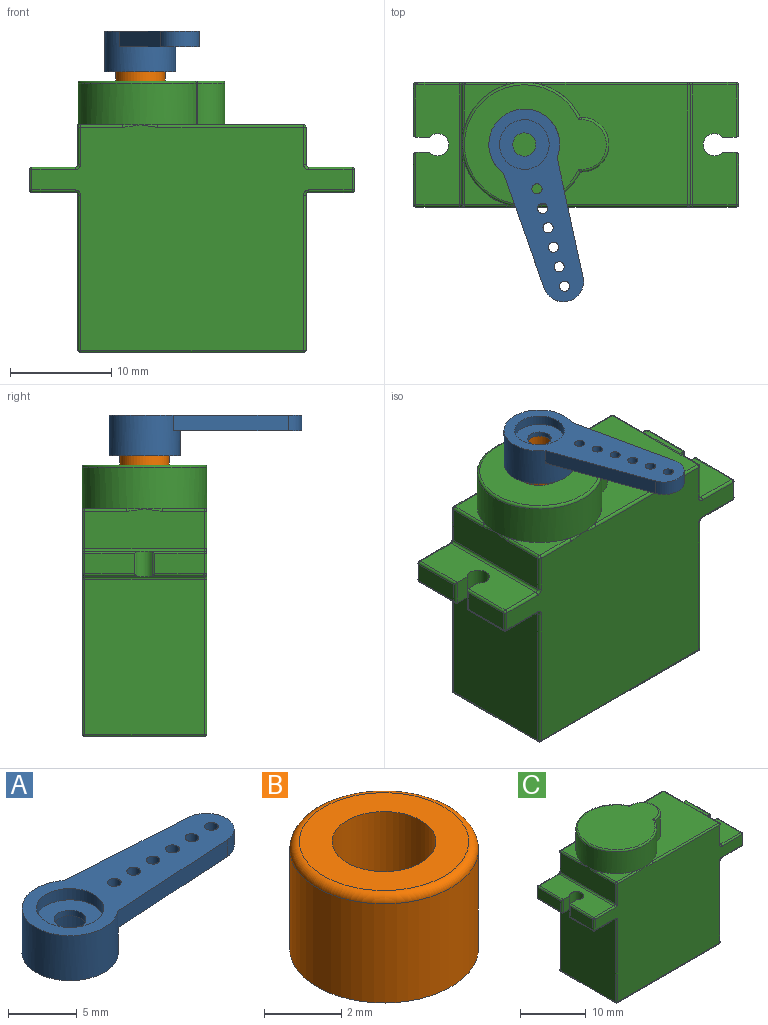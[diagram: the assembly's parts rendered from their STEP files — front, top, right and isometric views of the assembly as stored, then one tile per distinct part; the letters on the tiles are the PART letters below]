
ASSEMBLY  parts=3 mates=2
PART A: 18 faces, bbox 19.6x7x4 mm
  f0: plane 4.9x4.9mm, normal (0,0,-1), area 14.7mm2, adj f14,f16
  f1: plane 12.01x1.5mm, normal (0.06,1,0), area 18.1mm2, adj f2,f10,f12,f13
  f2: cylinder r=3.5mm len=7mm, axis (0,0,-1), area 78.5mm2, adj f1,f3,f12,f13,f17
  f3: plane 12.01x1.5mm, normal (0.06,-1,0), area 18.1mm2, adj f2,f10,f12,f13
  f4: cylinder r=0.5mm len=1.5mm, axis (0,0,-1), area 4.7mm2, adj f12,f13
  f5: cylinder r=0.5mm len=1.5mm, axis (0,0,-1), area 4.7mm2, adj f12,f13
  f6: cylinder r=0.5mm len=1.5mm, axis (0,0,-1), area 4.7mm2, adj f12,f13
  f7: cylinder r=0.5mm len=1.5mm, axis (0,0,-1), area 4.7mm2, adj f12,f13
  f8: cylinder r=0.5mm len=1.5mm, axis (0,0,-1), area 4.7mm2, adj f12,f13
  f9: cylinder r=0.5mm len=1.5mm, axis (0,0,-1), area 4.7mm2, adj f12,f13
  f10: cylinder r=2mm len=3.99mm, axis (0,0,-1), area 9mm2, adj f1,f3,f12,f13
  f11: cylinder r=2.45mm len=4.9mm, axis (0,0,-1), area 15.4mm2, adj f12,f15
  f12: plane 19.55x7mm, normal (0,0,1), area 72.6mm2, adj f1,f2,f3,f4,f5,f6,f7,f8
  f13: plane 13.89x5.5mm, normal (0,0,-1), area 53mm2, adj f1,f2,f3,f4,f5,f6,f7,f8
  f14: cylinder r=1.15mm len=2.3mm, axis (0,0,-1), area 3.6mm2, adj f0,f15
  f15: plane 4.9x4.9mm, normal (0,0,1), area 14.7mm2, adj f11,f14
  f16: cylinder r=2.45mm len=4.9mm, axis (0,0,1), area 38.5mm2, adj f0,f17
  f17: plane 7x7mm, normal (0,0,-1), area 19.6mm2, adj f2,f16
PART B: 5 faces, bbox 5.3x5.3x3.4 mm
  f0: cylinder r=1.35mm len=3.4mm, axis (0,0,-1), area 28.8mm2, adj f2,f3
  f1: cylinder r=2.45mm len=4.9mm, axis (0,0,-1), area 48.5mm2, adj f3,f4
  f2: plane 4.4x4.4mm, normal (0,0,1), area 9.5mm2, adj f0,f4
  f3: plane 4.9x4.9mm, normal (0,0,-1), area 13.1mm2, adj f0,f1
  f4: torus R=2.2mm, axis (0,0,1), area 5.8mm2, adj f1,f2
PART C: 110 faces, bbox 32.2x13.4x26.9 mm
  f0: plane 14.36x11.8mm, normal (0,0,1), area 121.3mm2, adj f24,f25,f26,f27,f34,f38,f39
  f1: plane 4.16x4.16mm, normal (0,0,1), area 5.7mm2, adj f25,f71,f72
  f2: plane 15.3x11.8mm, normal (-1,0,0), area 180.5mm2, adj f94,f95,f103,f104
  f3: plane 15.3x11.8mm, normal (1,0,0), area 180.5mm2, adj f68,f69,f85,f86
  f4: plane 11.86x4.01mm, normal (-1,0,0), area 44mm2, adj f56,f61,f66,f72,f73,f87,f88
  f5: plane 31.66x22.31mm, normal (0,-1,0), area 503.8mm2, adj f33,f34,f37,f40,f42,f49,f57,f58
  f6: plane 11.8x3.7mm, normal (1,0,0), area 43.7mm2, adj f37,f38,f44,f45
  f7: plane 31.66x22.31mm, normal (0,1,0), area 503.8mm2, adj f36,f39,f45,f48,f52,f60,f65,f70
  f8: plane 4.16x4.16mm, normal (0,0,1), area 5.7mm2, adj f25,f61,f62
  f9: plane 22x11.8mm, normal (0,0,-1), area 259.6mm2, adj f84,f85,f95,f96
  f10: plane 4.9x2mm, normal (1,0,0), area 9.8mm2, adj f51,f54,f59,f60
  f11: plane 2.5x1.35mm, normal (0,-1,0), area 3.4mm2, adj f12,f15,f16,f54
  f12: cylinder r=1.1mm len=2.5mm, axis (0,0,-1), area 13.2mm2, adj f11,f13,f15,f16
  f13: plane 2.5x1.35mm, normal (0,1,0), area 3.4mm2, adj f12,f15,f16,f47
  f14: plane 4.9x2mm, normal (1,0,0), area 9.8mm2, adj f43,f47,f49,f50
  f15: plane 11.8x4.3mm, normal (0,0,1), area 45.2mm2, adj f11,f12,f13,f42,f43,f44,f51,f52
  f16: plane 11.8x4.3mm, normal (0,0,-1), area 45.2mm2, adj f11,f12,f13,f50,f58,f59,f69,f70
  f17: plane 4.9x2mm, normal (-1,0,0), area 9.8mm2, adj f74,f76,f82,f83
  f18: plane 2.5x1.35mm, normal (0,1,0), area 3.4mm2, adj f19,f22,f23,f76
  f19: cylinder r=1.1mm len=2.5mm, axis (0,0,-1), area 13.2mm2, adj f18,f20,f22,f23
  f20: plane 2.5x1.35mm, normal (0,-1,0), area 3.4mm2, adj f19,f22,f23,f102
  f21: plane 4.9x2mm, normal (-1,0,0), area 9.8mm2, adj f98,f102,f105,f106
  f22: plane 11.8x4.3mm, normal (0,0,1), area 45.2mm2, adj f18,f19,f20,f74,f75,f88,f97,f98
  f23: plane 11.8x4.3mm, normal (0,0,-1), area 45.2mm2, adj f18,f19,f20,f82,f93,f103,f106,f109
  f24: plane 4.05x0.12mm, normal (0,1,0), area 0.5mm2, adj f0,f25,f27,f32
  f25: cylinder r=6.15mm len=12.3mm, axis (0,0,-1), area 133.9mm2, adj f0,f1,f8,f24,f26,f31,f33,f36
  f26: plane 4.05x0.12mm, normal (0,-1,0), area 0.5mm2, adj f0,f25,f27,f29
  f27: cylinder r=2.7mm len=5.4mm, axis (0,0,-1), area 34.4mm2, adj f0,f24,f26,f30
  f28: plane 14x11.8mm, normal (0,0,1), area 118.4mm2, adj f29,f30,f31,f32
  f29: cylinder r=0.25mm len=0.28mm, axis (-1,0,0), area 0.1mm2, adj f26,f28,f30,f31
  f30: torus R=2.45mm, axis (0,0,1), area 3.2mm2, adj f27,f28,f29,f32
  f31: torus R=5.9mm, axis (0,0,1), area 12.8mm2, adj f25,f28,f29,f32
  f32: cylinder r=0.25mm len=0.28mm, axis (1,0,0), area 0.1mm2, adj f24,f28,f30,f31
  f33: bspline ~1.82x0.28mm, area 0.2mm2, adj f5,f25,f34
  f34: cylinder r=0.25mm len=14.36mm, axis (-1,0,0), area 5.6mm2, adj f0,f5,f33,f35
  f35: sphere r=0.25mm, area 0.1mm2, adj f34,f37,f38
  f36: bspline ~1.82x0.28mm, area 0.2mm2, adj f7,f25,f39
  f37: cylinder r=0.25mm len=3.7mm, axis (0,0,-1), area 1.5mm2, adj f5,f6,f35,f40
  f38: cylinder r=0.25mm len=11.8mm, axis (0,-1,0), area 4.6mm2, adj f0,f6,f35,f41
  f39: cylinder r=0.25mm len=14.36mm, axis (1,0,0), area 5.6mm2, adj f0,f7,f36,f41
  f40: torus R=0.5mm, axis (0,1,0), area 0.2mm2, adj f5,f37,f42,f44
  f41: sphere r=0.25mm, area 0.1mm2, adj f38,f39,f45
  f42: cylinder r=0.25mm len=4.3mm, axis (1,0,0), area 1.7mm2, adj f5,f15,f40,f46
  f43: cylinder r=0.25mm len=5.15mm, axis (0,1,0), area 2mm2, adj f14,f15,f46,f47
  f44: cylinder r=0.25mm len=11.8mm, axis (0,-1,0), area 4.6mm2, adj f6,f15,f40,f48
  f45: cylinder r=0.25mm len=3.7mm, axis (0,0,1), area 1.5mm2, adj f6,f7,f41,f48
  f46: sphere r=0.25mm, area 0.1mm2, adj f42,f43,f49
  f47: cylinder r=0.25mm len=2.5mm, axis (0,0,-1), area 0.9mm2, adj f13,f14,f43,f50
  f48: torus R=0.5mm, axis (0,1,0), area 0.2mm2, adj f7,f44,f45,f52
  f49: cylinder r=0.25mm len=2mm, axis (0,0,-1), area 0.8mm2, adj f5,f14,f46,f53
  f50: cylinder r=0.25mm len=5.15mm, axis (0,-1,0), area 2mm2, adj f14,f16,f47,f53
  f51: cylinder r=0.25mm len=5.15mm, axis (0,1,0), area 2mm2, adj f10,f15,f54,f55
  f52: cylinder r=0.25mm len=4.3mm, axis (-1,0,0), area 1.7mm2, adj f7,f15,f48,f55
  f53: sphere r=0.25mm, area 0.1mm2, adj f49,f50,f58
  f54: cylinder r=0.25mm len=2.5mm, axis (0,0,-1), area 0.9mm2, adj f10,f11,f51,f59
  f55: sphere r=0.25mm, area 0.1mm2, adj f51,f52,f60
  f56: bspline ~1.82x0.28mm, area 0.2mm2, adj f4,f25,f61
  f57: bspline ~1.82x0.28mm, area 0.2mm2, adj f5,f25,f62
  f58: cylinder r=0.25mm len=4.3mm, axis (-1,0,0), area 1.7mm2, adj f5,f16,f53,f63
  f59: cylinder r=0.25mm len=5.15mm, axis (0,-1,0), area 2mm2, adj f10,f16,f54,f64
  f60: cylinder r=0.25mm len=2mm, axis (0,0,-1), area 0.8mm2, adj f7,f10,f55,f64
  f61: cylinder r=0.25mm len=4.16mm, axis (0,1,0), area 1.6mm2, adj f4,f8,f56,f67
  f62: cylinder r=0.25mm len=4.16mm, axis (-1,0,0), area 1.6mm2, adj f5,f8,f57,f67
  f63: torus R=0.5mm, axis (0,1,0), area 0.2mm2, adj f5,f58,f68,f69
  f64: sphere r=0.25mm, area 0.1mm2, adj f59,f60,f70
  f65: bspline ~1.82x0.28mm, area 0.2mm2, adj f7,f25,f71
  f66: bspline ~1.82x0.28mm, area 0.2mm2, adj f4,f25,f72
  f67: sphere r=0.25mm, area 0.1mm2, adj f61,f62,f73
  f68: cylinder r=0.25mm len=15.3mm, axis (0,0,-1), area 6mm2, adj f3,f5,f63,f78
  f69: cylinder r=0.25mm len=11.8mm, axis (0,1,0), area 4.6mm2, adj f3,f16,f63,f79
  f70: cylinder r=0.25mm len=4.3mm, axis (1,0,0), area 1.7mm2, adj f7,f16,f64,f79
  f71: cylinder r=0.25mm len=4.16mm, axis (1,0,0), area 1.6mm2, adj f1,f7,f65,f80
  f72: cylinder r=0.25mm len=4.16mm, axis (0,1,0), area 1.6mm2, adj f1,f4,f66,f80
  f73: cylinder r=0.25mm len=3.7mm, axis (0,0,1), area 1.5mm2, adj f4,f5,f67,f81
  f74: cylinder r=0.25mm len=5.15mm, axis (0,-1,0), area 2mm2, adj f17,f22,f76,f77
  f75: cylinder r=0.25mm len=4.3mm, axis (-1,0,0), area 1.7mm2, adj f5,f22,f77,f81
  f76: cylinder r=0.25mm len=2.5mm, axis (0,0,-1), area 0.9mm2, adj f17,f18,f74,f82
  f77: sphere r=0.25mm, area 0.1mm2, adj f74,f75,f83
  f78: sphere r=0.25mm, area 0.1mm2, adj f68,f84,f85
  f79: torus R=0.5mm, axis (0,1,0), area 0.2mm2, adj f7,f69,f70,f86
  f80: sphere r=0.25mm, area 0.1mm2, adj f71,f72,f87
  f81: torus R=0.5mm, axis (0,1,0), area 0.2mm2, adj f5,f73,f75,f88
  f82: cylinder r=0.25mm len=5.15mm, axis (0,1,0), area 2mm2, adj f17,f23,f76,f89
  f83: cylinder r=0.25mm len=2mm, axis (0,0,1), area 0.8mm2, adj f5,f17,f77,f89
  f84: cylinder r=0.25mm len=22mm, axis (1,0,0), area 8.6mm2, adj f5,f9,f78,f90
  f85: cylinder r=0.25mm len=11.8mm, axis (0,1,0), area 4.6mm2, adj f3,f9,f78,f91
  f86: cylinder r=0.25mm len=15.3mm, axis (0,0,1), area 6mm2, adj f3,f7,f79,f91
  f87: cylinder r=0.25mm len=3.7mm, axis (0,0,-1), area 1.5mm2, adj f4,f7,f80,f92
  f88: cylinder r=0.25mm len=11.8mm, axis (0,1,0), area 4.6mm2, adj f4,f22,f81,f92
  f89: sphere r=0.25mm, area 0.1mm2, adj f82,f83,f93
  f90: sphere r=0.25mm, area 0.1mm2, adj f84,f94,f95
  f91: sphere r=0.25mm, area 0.1mm2, adj f85,f86,f96
  f92: torus R=0.5mm, axis (0,1,0), area 0.2mm2, adj f7,f87,f88,f97
  f93: cylinder r=0.25mm len=4.3mm, axis (1,0,0), area 1.7mm2, adj f5,f23,f89,f99
  f94: cylinder r=0.25mm len=15.3mm, axis (0,0,1), area 6mm2, adj f2,f5,f90,f99
  f95: cylinder r=0.25mm len=11.8mm, axis (0,-1,0), area 4.6mm2, adj f2,f9,f90,f100
  f96: cylinder r=0.25mm len=22mm, axis (-1,0,0), area 8.6mm2, adj f7,f9,f91,f100
  f97: cylinder r=0.25mm len=4.3mm, axis (1,0,0), area 1.7mm2, adj f7,f22,f92,f101
  f98: cylinder r=0.25mm len=5.15mm, axis (0,-1,0), area 2mm2, adj f21,f22,f101,f102
  f99: torus R=0.5mm, axis (0,1,0), area 0.2mm2, adj f5,f93,f94,f103
  f100: sphere r=0.25mm, area 0.1mm2, adj f95,f96,f104
  f101: sphere r=0.25mm, area 0.1mm2, adj f97,f98,f105
  f102: cylinder r=0.25mm len=2.5mm, axis (0,0,-1), area 0.9mm2, adj f20,f21,f98,f106
  f103: cylinder r=0.25mm len=11.8mm, axis (0,-1,0), area 4.6mm2, adj f2,f23,f99,f107
  f104: cylinder r=0.25mm len=15.3mm, axis (0,0,-1), area 6mm2, adj f2,f7,f100,f107
  f105: cylinder r=0.25mm len=2mm, axis (0,0,1), area 0.8mm2, adj f7,f21,f101,f108
  f106: cylinder r=0.25mm len=5.15mm, axis (0,1,0), area 2mm2, adj f21,f23,f102,f108
  f107: torus R=0.5mm, axis (0,1,0), area 0.2mm2, adj f7,f103,f104,f109
  f108: sphere r=0.25mm, area 0.1mm2, adj f105,f106,f109
  f109: cylinder r=0.25mm len=4.3mm, axis (-1,0,0), area 1.7mm2, adj f7,f23,f107,f108
PLACE A rot(axis=(0,0,-1),74.1deg) t=(-1.7,10.38,-0.25)mm
PLACE B t=(-0.25,0,-0.25)mm
PLACE C t=(-0.25,0,-0.25)mm
MATE revolute B.f0 <-> C.f25  axis (0,0,-1) through (5.9,6.15,26.55)mm
MATE revolute A.f2 <-> B.f0  axis (0,0,-1) through (5.9,6.15,29.95)mm
